# Revit family: WC-Wall Faced-Caroma Liano Junior Cleanflush Suite
name_source: partatom
category: Plumbing Fixtures
revit_build: Autodesk Revit 2014 (Build: 20140709_2115(x64)
units: mm (PartAtom-declared; Revit-internal decimal feet)

## types (1)
- Caroma Liano Junior Cleanflush Wall Faced Suite
    Assembly Code = D2010110
    CW Connection = Yes
    CWFU = 2
    Default Elevation = 0 mm  [stored 0 ft]
    Description = Liano Vitreous China Wall Faced Pan and Close Coupled Cistern
    HW Connection = No
    Hardware = Metal-Chrome-Caroma
    Height_ANZRS = 766 mm  [stored 2.51312 ft]
    Keynote = WC
    Length_ANZRS = 338 mm  [stored 1.10892 ft]
    Manufacturer = GWA Bathrooms & Kitchens
    Material_ANZRS = Porcelain-White-Caroma
    Model = 767000W
    ModifiedIssue_ANZRS = 20160909.01 $
    Type Comments = Caroma Liano Junior Cleanflush Wall Faced Suite with Back Inlet Pan, Close Coupled Cistern and Seat
    URL = http://specify.caroma.com.au
    Vent Connection = No
    WELSRating_ANZRS = 4
    WFU = 3
    Waste Connection = Yes
    Width_ANZRS = 602 mm  [stored 1.97507 ft]

note: [stored X ft] marks values corroborated as IEEE doubles in the binary element streams (Revit-internal decimal feet)

## geometry (parser evidence)
native form markers: Blend x8, Sweep x1
no freeform markers — native parametric forms only
